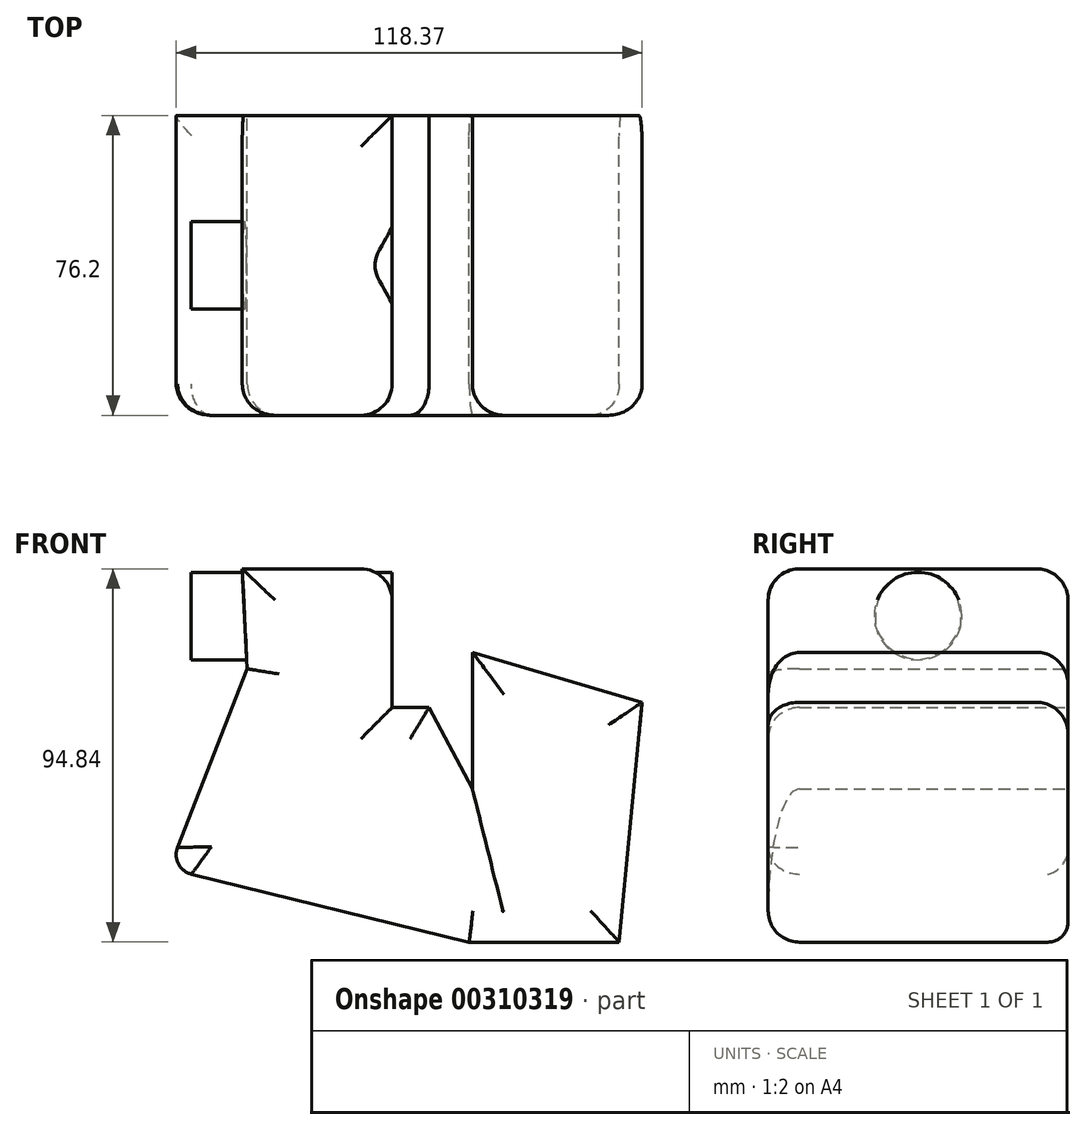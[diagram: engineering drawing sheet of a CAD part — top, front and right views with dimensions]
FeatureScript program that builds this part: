
annotation { "Feature Type Name" : "Feature", "Feature Type Description" : "" }
export const myFeature = defineFeature(function(context is Context, id is Id, definition is map)
    precondition{}
    {
        {
            var Q0;
            Q0=qCreatedBy(makeId("Front.planeOp"),FACE);
            var sketch = newSketch(context, id + "F0", { "sketchPlane" : qUnion([Q0])});
            skLineSegment(sketch, "E0", {"start": v(0, 65.25) * mm, "end": v(-38.1, 65.25) * mm});
            skLineSegment(sketch, "E1", {"start": v(-38.1, 65.25) * mm, "end": v(-36.82, 39.85) * mm});
            skLineSegment(sketch, "E2", {"start": v(-36.82, 39.85) * mm, "end": v(-56.63, -10.95) * mm});
            skLineSegment(sketch, "E3", {"start": v(-56.63, -10.95) * mm, "end": v(19.57, -29.6) * mm});
            skLineSegment(sketch, "E4", {"start": v(19.57, -29.6) * mm, "end": v(57.67, -29.6) * mm});
            skLineSegment(sketch, "E5", {"start": v(57.67, -29.6) * mm, "end": v(63.5, 31.34) * mm});
            skLineSegment(sketch, "E6", {"start": v(63.5, 31.34) * mm, "end": v(20.39, 44.04) * mm});
            skLineSegment(sketch, "E7", {"start": v(20.39, 44.04) * mm, "end": v(20.39, 9.32) * mm});
            skLineSegment(sketch, "E8", {"start": v(20.39, 9.32) * mm, "end": v(9.36, 30.02) * mm});
            skLineSegment(sketch, "E9", {"start": v(9.36, 30.02) * mm, "end": v(0, 30.02) * mm});
            skLineSegment(sketch, "E10", {"start": v(0, 30.02) * mm, "end": v(0, 65.25) * mm});
            skSolve(sketch);
        }
        {
            var Q0;
            Q0=makeQuery(id+"F0.imprint","IMPRINT",FACE,{"disambiguationData":[TD([[makeQuery(id+"F0.imprint","IMPRINT",EDGE,{"derivedFrom":sQuery(id+"F0.wireOp",EDGE,"E0")}),1.0]])]});
            extrude(context, id + "F1", {"entities" : qUnion([Q0]), "endBound" : BoundingType.SYMMETRIC, "depth" : 76.2 * mm});
        }
        {
            var Q0;
            Q0=makeQuery(id+"F1.opExtrude","CAP_FACE",FACE,{"disambiguationData":[OSD([sQuery(id+"F0.wireOp",EDGE,"E0"),sQuery(id+"F0.wireOp",EDGE,"E1"),sQuery(id+"F0.wireOp",EDGE,"E2"),sQuery(id+"F0.wireOp",EDGE,"E3"),sQuery(id+"F0.wireOp",EDGE,"E4"),sQuery(id+"F0.wireOp",EDGE,"E5"),sQuery(id+"F0.wireOp",EDGE,"E6"),sQuery(id+"F0.wireOp",EDGE,"E7"),sQuery(id+"F0.wireOp",EDGE,"E8"),sQuery(id+"F0.wireOp",EDGE,"E9"),sQuery(id+"F0.wireOp",EDGE,"E10")])],"isStart":false});
            var Q1;
            Q1=makeQuery(id+"F1.opExtrude","CAP_EDGE",EDGE,{"disambiguationData":[OSD([sQuery(id+"F0.wireOp",EDGE,"E6")])],"isStart":true});
            var Q2;
            Q2=makeQuery(id+"F1.opExtrude","SWEPT_EDGE",EDGE,{"disambiguationData":[OSD([sQuery(id+"F0.wireOp",EDGE,"E0"),sQuery(id+"F0.wireOp",EDGE,"E10")])]});
            var Q3;
            Q3=makeQuery(id+"F1.opExtrude","CAP_EDGE",EDGE,{"disambiguationData":[OSD([sQuery(id+"F0.wireOp",EDGE,"E0")])],"isStart":true});
            fillet(context, id + "F2", {"entities" : qUnion([Q0, Q1, Q2, Q3]), "radius" : 7.97 * mm, "tangentPropagation" : true, "allowEdgeOverflow" : false});
        }
        {
            var Q0;
            Q0=makeQuery(id+"F1.opExtrude","SWEPT_EDGE",EDGE,{"disambiguationData":[OSD([sQuery(id+"F0.wireOp",EDGE,"E2"),sQuery(id+"F0.wireOp",EDGE,"E3")])]});
            var Q1;
            Q1=makeQuery(id+"F1.opExtrude","CAP_EDGE",EDGE,{"disambiguationData":[OSD([sQuery(id+"F0.wireOp",EDGE,"E3")])],"isStart":true});
            var Q2;
            {var subQ0=sQuery(id+"F0.wireOp",EDGE,"E3");Q2=makeQuery(id+"F2.opFillet","BLEND_EDGE",EDGE,{"blendedFrom":[makeQuery(id+"F1.opExtrude","CAP_EDGE",EDGE,{"disambiguationData":[OSD([subQ0])],"isStart":false}),makeQuery(id+"F1.opExtrude","SWEPT_FACE",FACE,{"disambiguationData":[OSD([subQ0])]})],"blendedInto":[makeQuery(id+"F1.opExtrude","SWEPT_FACE",FACE,{"disambiguationData":[OSD([subQ0])]})]});}
            var Q3;
            Q3=makeQuery(id+"F1.opExtrude","CAP_EDGE",EDGE,{"disambiguationData":[OSD([sQuery(id+"F0.wireOp",EDGE,"E4")])],"isStart":true});
            fillet(context, id + "F3", {"entities" : qUnion([Q0, Q1, Q2, Q3]), "radius" : 5.08 * mm, "tangentPropagation" : true, "allowEdgeOverflow" : false});
        }
        {
            var Q0;
            Q0=qCreatedBy(makeId("Right.planeOp"),FACE);
            var sketch = newSketch(context, id + "F4", { "sketchPlane" : qUnion([Q0])});
            skCircle(sketch, "E11", {"center": v(0, 53.25) * mm, "radius": 11.13 * mm});
            skSolve(sketch);
        }
        {
            var Q0;
            Q0=makeQuery(id+"F4.imprint","IMPRINT",FACE,{"disambiguationData":[TD([[makeQuery(id+"F4.imprint","IMPRINT",EDGE,{"derivedFrom":sQuery(id+"F4.wireOp",EDGE,"E11")}),1.0]])]});
            extrude(context, id + "F5", {"entities" : qUnion([Q0]), "operationType" : NewBodyOperationType.ADD, "oppositeDirection" : true, "depth" : 51.05 * mm});
        }
    });
